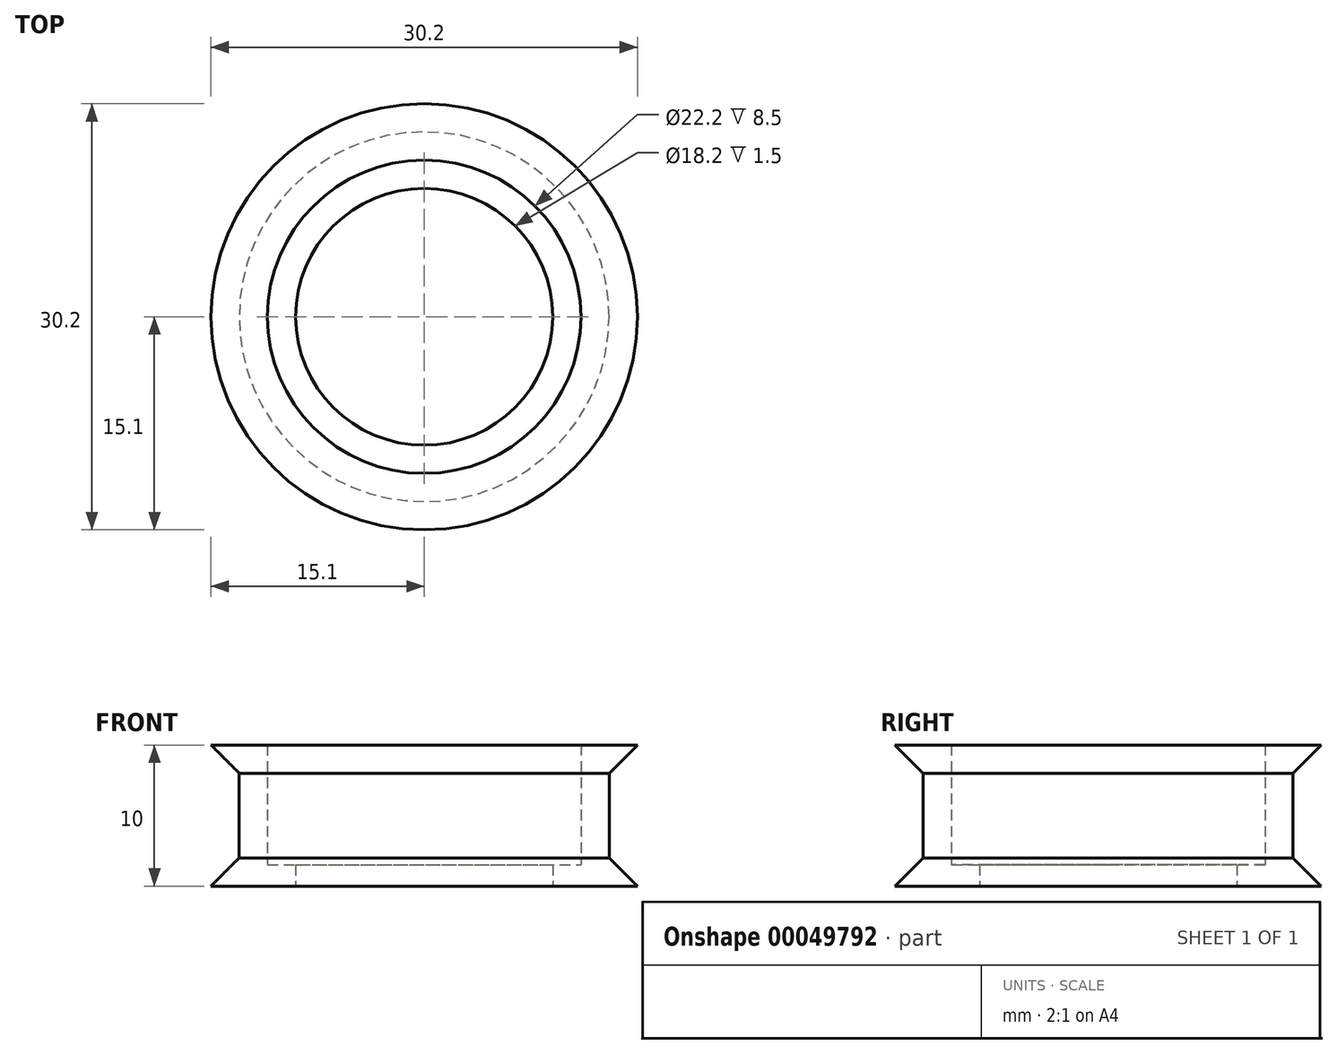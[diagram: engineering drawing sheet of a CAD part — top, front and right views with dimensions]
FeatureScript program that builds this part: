
annotation { "Feature Type Name" : "Feature", "Feature Type Description" : "" }
export const myFeature = defineFeature(function(context is Context, id is Id, definition is map)
    precondition{}
    {
        {
            var Q0;
            Q0=qCreatedBy(makeId("Front.planeOp"),FACE);
            var sketch = newSketch(context, id + "F0", { "sketchPlane" : qUnion([Q0])});
            skLineSegment(sketch, "E0", {"start": v(11.1, 4.8) * mm, "end": v(15.1, 4.8) * mm});
            skLineSegment(sketch, "E1", {"start": v(15.1, 4.8) * mm, "end": v(13.1, 2.8) * mm});
            skLineSegment(sketch, "E2", {"start": v(13.1, 2.8) * mm, "end": v(13.1, -3.2) * mm});
            skLineSegment(sketch, "E3", {"start": v(13.1, -3.2) * mm, "end": v(15.1, -5.2) * mm});
            skLineSegment(sketch, "E4", {"start": v(15.1, -5.2) * mm, "end": v(11.1, -5.2) * mm});
            skLineSegment(sketch, "E5", {"start": v(11.1, -5.2) * mm, "end": v(11.1, 4.8) * mm});
            skLineSegment(sketch, "E6", {"start": v(0, -3.77) * mm, "end": v(0, 4.95) * mm, "construction": true});
            skLineSegment(sketch, "E7.bottom", {"start": v(11.1, -5.2) * mm, "end": v(9.1, -5.2) * mm});
            skLineSegment(sketch, "E7.top", {"start": v(11.1, -3.7) * mm, "end": v(9.1, -3.7) * mm});
            skLineSegment(sketch, "E7.left", {"start": v(11.1, -5.2) * mm, "end": v(11.1, -3.7) * mm});
            skLineSegment(sketch, "E7.right", {"start": v(9.1, -5.2) * mm, "end": v(9.1, -3.7) * mm});
            skSolve(sketch);
        }
        {
            var Q0;
            Q0=qSketchRegion(id+"F0",true);
            var Q1;
            Q1=sQuery(id+"F0.wireOp",EDGE,"E6");
            revolve(context, id + "F1", {"entities" : qUnion([Q0]), "axis" : qUnion([Q1]), "revolveType" : RevolveType.FULL});
        }
    });
